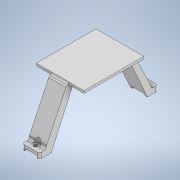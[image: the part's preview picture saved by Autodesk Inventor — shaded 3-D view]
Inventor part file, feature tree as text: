
AUTODESK INVENTOR PART (.ipt)
format: ipt  version: 2022 (Build 260153000, 153)  size: 305,152 bytes
history: native  units: in
note: dims shown in document units (in); Inventor stores cm internally (conversion verified against a paired STEP export)
features: sketch x8, extrude x7, fillet x3, hole x1
ambient origin geometry x8: Origin, YZ Plane, XZ Plane, XY Plane, X Axis, Y Axis, Z Axis, Center Point
bodies: Solid1 (feature_tree)
feature tree (19):
  extrude  "Extrusion1"  Depth=3.7559in
  extrude  "Extrusion2"  Depth=1.5748in
  fillet  "Fillet1"  Radius=1.9685in
  extrude  "Extrusion3"  Depth=0.502in
  hole  "Hole1"  [1 undecoded]
  fillet  "Fillet3"  Radius=0.1575in
  extrude  "Extrusion7"  Depth=0.1575in
  extrude  "Extrusion8"  Depth=0.4515in
  extrude  "Extrusion9"  TaperAngle=0.0deg  [1 undecoded]
  extrude  "Extrusion10"  Depth=0.0787in
  fillet  "Fillet5"  Radius=0.0787in
  sketch  "Sketch1"  dims[d0=0.5709in d1=3.7559in]
  sketch  "Sketch2"  dims[d2=1.6535in d3=0.0in d4=1.5748in d5=1.9685in]
  sketch  "Sketch3"  dims[d6=0.8937in d7=0.502in]
  sketch  "Sketch4"  dims[d8=0.0787in d9=0.0in d10=0.0787in d11=0.1575in]
  sketch  "Sketch8"  dims[d12=1.378in d13=0.1575in]
  sketch  "Sketch10"  dims[d14=1.378in d15=0.4515in]
  sketch  "Sketch11"  dims[d16=0.7853in d17=0.0in d18=0.0in]
  sketch  "Sketch12"  dims[d19=0.1181in d20=0.2362in d21=0.1181in d22=0.0394in d23=90.0deg d24=0.315in d25=0.8108in d33=0.0787in d38=0.0787in d39=0.0in d40=0.0787in d41=0.0in d42=0.4134in d43=0.0787in d44=0.0787in d45=0.1969in d46=0.0in d47=0.0in d49=0.2362in d50=0.2362in d51=0.1969in d52=0.0in d53=0.0787in]
note: 2 required parameter values undecoded (feature->parameter linkage not recoverable at this tier; creation-order binding heuristic only, values carry confidence <= 0.55)
